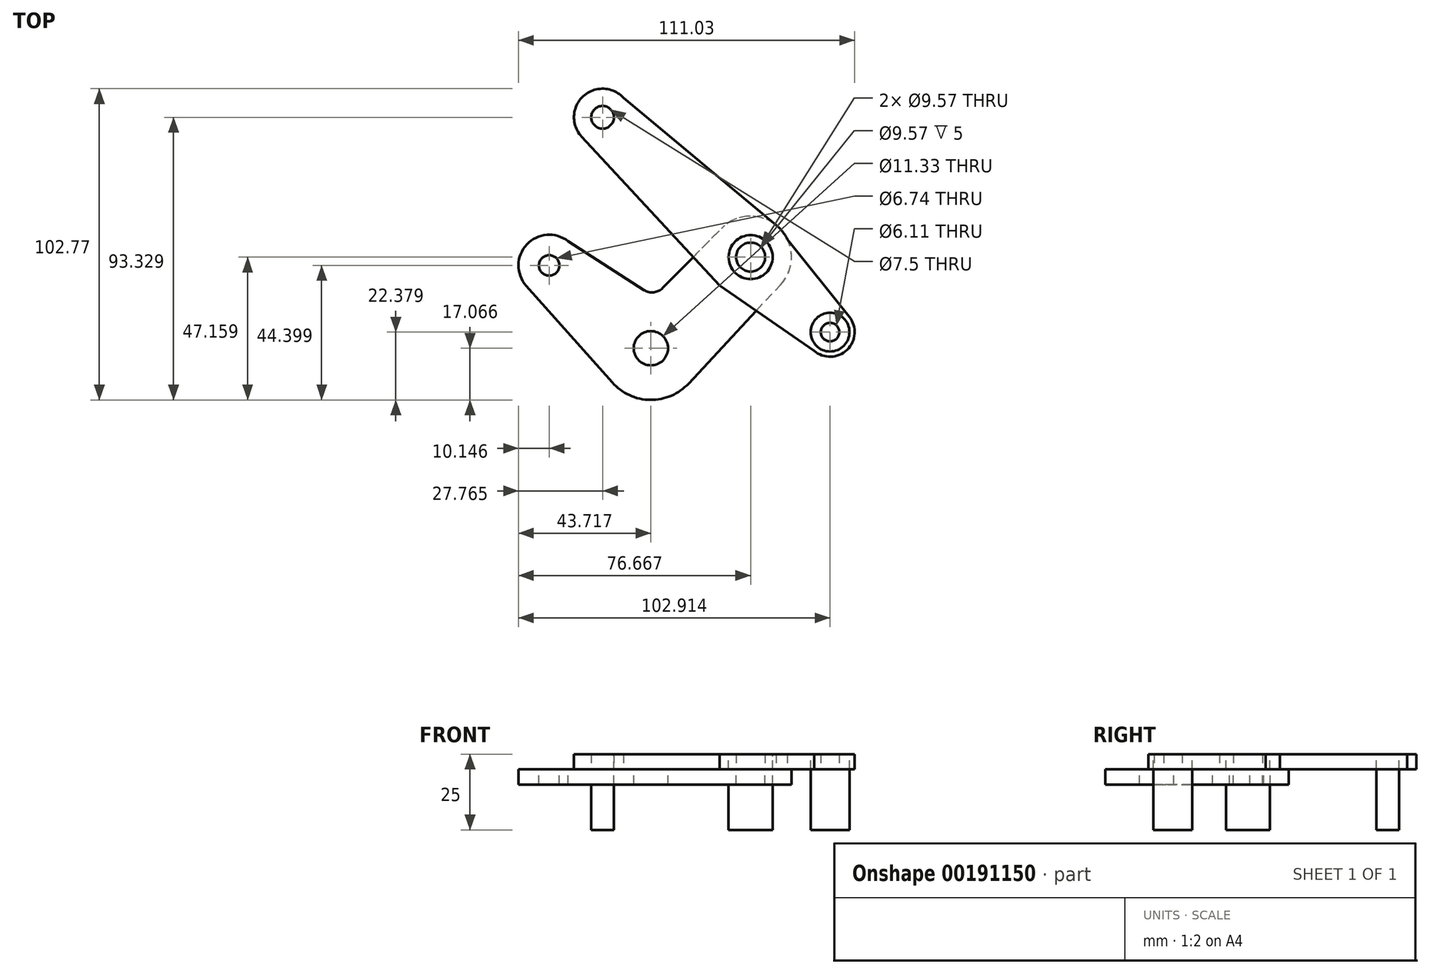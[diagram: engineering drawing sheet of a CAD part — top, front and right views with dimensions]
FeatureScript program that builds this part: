
annotation { "Feature Type Name" : "Feature", "Feature Type Description" : "" }
export const myFeature = defineFeature(function(context is Context, id is Id, definition is map)
    precondition{}
    {
        {
            var Q0;
            Q0=qCreatedBy(makeId("Top.planeOp"),FACE);
            var sketch = newSketch(context, id + "F0", { "sketchPlane" : qUnion([Q0])});
            skCircle(sketch, "E0", {"center": v(-58, -13.34) * mm, "radius": 10.15 * mm});
            skLineSegment(sketch, "E1", {"start": v(-58, -13.34) * mm, "end": v(-24.43, -40.67) * mm, "construction": true});
            skCircle(sketch, "E2", {"center": v(-24.43, -40.67) * mm, "radius": 17.06 * mm});
            skLineSegment(sketch, "E3", {"start": v(-65.59, -20.09) * mm, "end": v(-37.18, -52.02) * mm});
            skLineSegment(sketch, "E4", {"start": v(-24.43, -40.67) * mm, "end": v(8.52, -10.58) * mm, "construction": true});
            skCircle(sketch, "E5", {"center": v(8.52, -10.58) * mm, "radius": 13.5 * mm});
            skLineSegment(sketch, "E6", {"start": v(-11.93, -52.29) * mm, "end": v(10.37, -28.28) * mm});
            skLineSegment(sketch, "E7", {"start": v(-51.76, -5.34) * mm, "end": v(-26.75, -21.45) * mm});
            skLineSegment(sketch, "E8", {"start": v(-20.48, -20.76) * mm, "end": v(-10.4, -10.55) * mm});
            skPoint(sketch, "E9.visualSharp", {"position": v(-23.33, -23.65) * mm});
            skArc(sketch, "E9.filletArc", {"start": v(-26.75, -21.45) * mm, "mid": v(-23.5, -22.21) * mm, "end": v(-20.48, -20.76) * mm});
            skLineSegment(sketch, "E10", {"start": v(8.52, -10.58) * mm, "end": v(-40.39, 35.59) * mm, "construction": true});
            skLineSegment(sketch, "E11", {"start": v(8.52, -10.58) * mm, "end": v(34.76, -35.36) * mm, "construction": true});
            skCircle(sketch, "E12", {"center": v(-40.39, 35.59) * mm, "radius": 9.45 * mm});
            skCircle(sketch, "E13", {"center": v(34.76, -35.36) * mm, "radius": 8.11 * mm});
            skLineSegment(sketch, "E14", {"start": v(-33.44, 41.99) * mm, "end": v(16.9, 0) * mm});
            skLineSegment(sketch, "E15", {"start": v(16.9, 0) * mm, "end": v(41.1, -30.3) * mm});
            skLineSegment(sketch, "E16", {"start": v(29.45, -41.5) * mm, "end": v(-1.7, -19.92) * mm});
            skLineSegment(sketch, "E17", {"start": v(-47.3, 29.16) * mm, "end": v(-1.7, -19.92) * mm});
            skLineSegment(sketch, "E18.trimOffspring", {"start": v(-1.3, -1.31) * mm, "end": v(0, 0) * mm});
            skLineSegment(sketch, "E19", {"start": v(-10.4, -10.55) * mm, "end": v(-1.3, -1.31) * mm});
            skLineSegment(sketch, "E20", {"start": v(10.37, -28.28) * mm, "end": v(18.33, -19.84) * mm});
            skCircle(sketch, "E21", {"center": v(-58, -13.34) * mm, "radius": 3.37 * mm});
            skCircle(sketch, "E22", {"center": v(-24.43, -40.67) * mm, "radius": 5.67 * mm});
            skCircle(sketch, "E23", {"center": v(8.52, -10.58) * mm, "radius": 4.78 * mm});
            skCircle(sketch, "E24", {"center": v(34.76, -35.36) * mm, "radius": 3.06 * mm});
            skCircle(sketch, "E25", {"center": v(-40.39, 35.59) * mm, "radius": 3.75 * mm});
            skSolve(sketch);
        }
        {
            var Q0;
            {var subQ0=sQuery(id+"F0.wireOp",EDGE,"E15");var subQ1=sQuery(id+"F0.wireOp",EDGE,"E5");var subQ2=makeQuery(id+"F0.imprint","INTERSECT",VERTEX,{"disambiguationData":[OD(0.0)],"derivedFrom":[subQ1,subQ0]});Q0=makeQuery(id+"F0.imprint","IMPRINT",FACE,{"disambiguationData":[TD([[makeQuery(id+"F0.imprint","IMPRINT",EDGE,{"disambiguationData":[TD([[subQ2,1.0]])],"derivedFrom":subQ1}),1.0]])]});}
            var Q1;
            {var subQ0=sQuery(id+"F0.wireOp",EDGE,"E12");var subQ1=makeQuery(id+"F0.imprint","INTERSECT",VERTEX,{"derivedFrom":[subQ0,sQuery(id+"F0.wireOp",EDGE,"E14")]});Q1=makeQuery(id+"F0.imprint","IMPRINT",FACE,{"disambiguationData":[TD([[makeQuery(id+"F0.imprint","IMPRINT",EDGE,{"disambiguationData":[TD([[subQ1,-1.0]])],"derivedFrom":subQ0}),1.0]])]});}
            var Q2;
            {var subQ0=sQuery(id+"F0.wireOp",EDGE,"E13");var subQ1=makeQuery(id+"F0.imprint","INTERSECT",VERTEX,{"derivedFrom":[subQ0,sQuery(id+"F0.wireOp",EDGE,"E15")]});Q2=makeQuery(id+"F0.imprint","IMPRINT",FACE,{"disambiguationData":[TD([[makeQuery(id+"F0.imprint","IMPRINT",EDGE,{"disambiguationData":[TD([[subQ1,-1.0]])],"derivedFrom":subQ0}),1.0]])]});}
            var Q3;
            {var subQ1=sQuery(id+"F0.wireOp",EDGE,"E14");Q3=makeQuery(id+"F0.imprint","IMPRINT",FACE,{"disambiguationData":[TD([[makeQuery(id+"F0.imprint","IMPRINT",EDGE,{"derivedFrom":subQ1}),-1.0]])]});}
            var Q4;
            {var subQ0=sQuery(id+"F0.wireOp",EDGE,"E20");Q4=makeQuery(id+"F0.imprint","IMPRINT",FACE,{"disambiguationData":[TD([[makeQuery(id+"F0.imprint","IMPRINT",EDGE,{"derivedFrom":subQ0}),1.0]])]});}
            var Q5;
            {var subQ7=sQuery(id+"F0.wireOp",EDGE,"E20");Q5=makeQuery(id+"F0.imprint","IMPRINT",FACE,{"disambiguationData":[TD([[makeQuery(id+"F0.imprint","IMPRINT",EDGE,{"derivedFrom":subQ7}),-1.0]])]});}
            var Q6;
            {var subQ0=sQuery(id+"F0.wireOp",EDGE,"E5");var subQ2=sQuery(id+"F0.wireOp",EDGE,"E15");var subQ6=makeQuery(id+"F0.imprint","INTERSECT",VERTEX,{"disambiguationData":[OD(0.0)],"derivedFrom":[subQ0,subQ2]});Q6=makeQuery(id+"F0.imprint","IMPRINT",FACE,{"disambiguationData":[TD([[makeQuery(id+"F0.imprint","IMPRINT",EDGE,{"disambiguationData":[TD([[subQ6,-1.0]])],"derivedFrom":subQ0}),1.0]])]});}
            var Q7;
            {var subQ0=sQuery(id+"F0.wireOp",EDGE,"E19");Q7=makeQuery(id+"F0.imprint","IMPRINT",FACE,{"disambiguationData":[TD([[makeQuery(id+"F0.imprint","IMPRINT",EDGE,{"derivedFrom":subQ0}),-1.0]])]});}
            extrude(context, id + "F1", {"entities" : qUnion([Q0, Q1, Q2, Q3, Q4, Q5, Q6, Q7]), "depth" : 5 * mm});
        }
        {
            var Q0;
            {var subQ0=sQuery(id+"F0.wireOp",EDGE,"E2");var subQ1=makeQuery(id+"F0.imprint","INTERSECT",VERTEX,{"derivedFrom":[subQ0,sQuery(id+"F0.wireOp",EDGE,"E3")]});Q0=makeQuery(id+"F0.imprint","IMPRINT",FACE,{"disambiguationData":[TD([[makeQuery(id+"F0.imprint","IMPRINT",EDGE,{"disambiguationData":[TD([[subQ1,-1.0]])],"derivedFrom":subQ0}),1.0]])]});}
            var Q1;
            {var subQ0=sQuery(id+"F0.wireOp",EDGE,"E15");var subQ1=sQuery(id+"F0.wireOp",EDGE,"E5");var subQ2=makeQuery(id+"F0.imprint","INTERSECT",VERTEX,{"disambiguationData":[OD(0.0)],"derivedFrom":[subQ1,subQ0]});Q1=makeQuery(id+"F0.imprint","IMPRINT",FACE,{"disambiguationData":[TD([[makeQuery(id+"F0.imprint","IMPRINT",EDGE,{"disambiguationData":[TD([[subQ2,1.0]])],"derivedFrom":subQ1}),1.0]])]});}
            var Q2;
            {var subQ0=sQuery(id+"F0.wireOp",EDGE,"E19");Q2=makeQuery(id+"F0.imprint","IMPRINT",FACE,{"disambiguationData":[TD([[makeQuery(id+"F0.imprint","IMPRINT",EDGE,{"derivedFrom":subQ0}),-1.0]])]});}
            var Q3;
            {var subQ0=sQuery(id+"F0.wireOp",EDGE,"E20");Q3=makeQuery(id+"F0.imprint","IMPRINT",FACE,{"disambiguationData":[TD([[makeQuery(id+"F0.imprint","IMPRINT",EDGE,{"derivedFrom":subQ0}),1.0]])]});}
            var Q4;
            {var subQ1=sQuery(id+"F0.wireOp",EDGE,"E3");Q4=makeQuery(id+"F0.imprint","IMPRINT",FACE,{"disambiguationData":[TD([[makeQuery(id+"F0.imprint","IMPRINT",EDGE,{"derivedFrom":subQ1}),1.0]])]});}
            var Q5;
            {var subQ0=sQuery(id+"F0.wireOp",EDGE,"E5");var subQ2=sQuery(id+"F0.wireOp",EDGE,"E15");var subQ6=makeQuery(id+"F0.imprint","INTERSECT",VERTEX,{"disambiguationData":[OD(0.0)],"derivedFrom":[subQ0,subQ2]});Q5=makeQuery(id+"F0.imprint","IMPRINT",FACE,{"disambiguationData":[TD([[makeQuery(id+"F0.imprint","IMPRINT",EDGE,{"disambiguationData":[TD([[subQ6,-1.0]])],"derivedFrom":subQ0}),1.0]])]});}
            var Q6;
            {var subQ0=sQuery(id+"F0.wireOp",EDGE,"E0");var subQ1=makeQuery(id+"F0.imprint","INTERSECT",VERTEX,{"derivedFrom":[subQ0,sQuery(id+"F0.wireOp",EDGE,"E3")]});Q6=makeQuery(id+"F0.imprint","IMPRINT",FACE,{"disambiguationData":[TD([[makeQuery(id+"F0.imprint","IMPRINT",EDGE,{"disambiguationData":[TD([[subQ1,1.0]])],"derivedFrom":subQ0}),1.0]])]});}
            extrude(context, id + "F2", {"entities" : qUnion([Q0, Q1, Q2, Q3, Q4, Q5, Q6]), "oppositeDirection" : true, "depth" : 5 * mm});
        }
        {
            var Q0;
            Q0=makeQuery(id+"F1.opExtrude","CAP_FACE",FACE,{"disambiguationData":[OSD([sQuery(id+"F0.wireOp",EDGE,"E5"),sQuery(id+"F0.wireOp",EDGE,"E12"),sQuery(id+"F0.wireOp",EDGE,"E13"),sQuery(id+"F0.wireOp",EDGE,"E14"),sQuery(id+"F0.wireOp",EDGE,"E15"),sQuery(id+"F0.wireOp",EDGE,"E16"),sQuery(id+"F0.wireOp",EDGE,"E17"),sQuery(id+"F0.wireOp",EDGE,"E23"),sQuery(id+"F0.wireOp",EDGE,"E24"),sQuery(id+"F0.wireOp",EDGE,"E25")])],"isStart":false});
            var sketch = newSketch(context, id + "F3", { "sketchPlane" : qUnion([Q0])});
            skCircle(sketch, "E26", {"center": v(-40.39, 35.59) * mm, "radius": 5.12 * mm});
            skCircle(sketch, "E27", {"center": v(8.52, -10.58) * mm, "radius": 7.26 * mm});
            skCircle(sketch, "E28", {"center": v(34.76, -35.36) * mm, "radius": 6.4 * mm});
            skSolve(sketch);
        }
        {
            var Q0;
            Q0=makeQuery(id+"F3.imprint","IMPRINT",FACE,{"disambiguationData":[TD([[makeQuery(id+"F3.imprint","IMPRINT",EDGE,{"derivedFrom":makeQuery(id+"F1.opExtrude","CAP_EDGE",EDGE,{"disambiguationData":[OSD([sQuery(id+"F0.wireOp",EDGE,"E23")])],"isStart":false})}),1.0]])]});
            var Q1;
            Q1=makeQuery(id+"F3.imprint","IMPRINT",FACE,{"disambiguationData":[TD([[makeQuery(id+"F3.imprint","IMPRINT",EDGE,{"derivedFrom":makeQuery(id+"F1.opExtrude","CAP_EDGE",EDGE,{"disambiguationData":[OSD([sQuery(id+"F0.wireOp",EDGE,"E24")])],"isStart":false})}),1.0]])]});
            var Q2;
            Q2=makeQuery(id+"F3.imprint","IMPRINT",FACE,{"disambiguationData":[TD([[makeQuery(id+"F3.imprint","IMPRINT",EDGE,{"derivedFrom":makeQuery(id+"F1.opExtrude","CAP_EDGE",EDGE,{"disambiguationData":[OSD([sQuery(id+"F0.wireOp",EDGE,"E25")])],"isStart":false})}),1.0]])]});
            var Q3;
            Q3=makeQuery(id+"F3.imprint","IMPRINT",FACE,{"disambiguationData":[TD([[makeQuery(id+"F3.imprint","IMPRINT",EDGE,{"derivedFrom":sQuery(id+"F3.wireOp",EDGE,"E27")}),1.0]])]});
            var Q4;
            Q4=makeQuery(id+"F3.imprint","IMPRINT",FACE,{"disambiguationData":[TD([[makeQuery(id+"F3.imprint","IMPRINT",EDGE,{"derivedFrom":sQuery(id+"F3.wireOp",EDGE,"E28")}),1.0]])]});
            extrude(context, id + "F4", {"entities" : qUnion([Q0, Q1, Q2, Q3, Q4]), "oppositeDirection" : true, "depth" : 25 * mm});
        }
        {
            var Q0;
            Q0=makeQuery(id+"F1.opExtrude","SWEPT_BODY",BODY,{"disambiguationData":[OSD([sQuery(id+"F0.wireOp",EDGE,"E5"),sQuery(id+"F0.wireOp",EDGE,"E12"),sQuery(id+"F0.wireOp",EDGE,"E13"),sQuery(id+"F0.wireOp",EDGE,"E14"),sQuery(id+"F0.wireOp",EDGE,"E15"),sQuery(id+"F0.wireOp",EDGE,"E16"),sQuery(id+"F0.wireOp",EDGE,"E17"),sQuery(id+"F0.wireOp",EDGE,"E23"),sQuery(id+"F0.wireOp",EDGE,"E24"),sQuery(id+"F0.wireOp",EDGE,"E25")])]});
            var Q1;
            Q1=makeQuery(id+"F4.opExtrude","SWEPT_BODY",BODY,{"disambiguationData":[OSD([sQuery(id+"F3.wireOp",EDGE,"E27")])]});
            var Q2;
            Q2=makeQuery(id+"F2.opExtrude","SWEPT_BODY",BODY,{"disambiguationData":[OSD([sQuery(id+"F0.wireOp",EDGE,"E0"),sQuery(id+"F0.wireOp",EDGE,"E2"),sQuery(id+"F0.wireOp",EDGE,"E3"),sQuery(id+"F0.wireOp",EDGE,"E5"),sQuery(id+"F0.wireOp",EDGE,"E6"),sQuery(id+"F0.wireOp",EDGE,"E7"),sQuery(id+"F0.wireOp",EDGE,"E8"),sQuery(id+"F0.wireOp",EDGE,"E9.filletArc"),sQuery(id+"F0.wireOp",EDGE,"E18.trimOffspring"),sQuery(id+"F0.wireOp",EDGE,"E19"),sQuery(id+"F0.wireOp",EDGE,"E20"),sQuery(id+"F0.wireOp",EDGE,"E21"),sQuery(id+"F0.wireOp",EDGE,"E22"),sQuery(id+"F0.wireOp",EDGE,"E23")])]});
            booleanBodies(context, id + "F5", {"operationType" : BooleanOperationType.INTERSECTION, "tools" : qUnion([Q0, Q1]), "targets" : qUnion([Q2]), "keepTools" : true});
        }
    });
